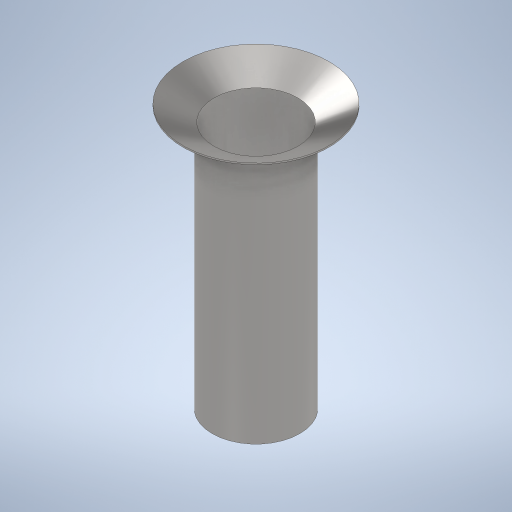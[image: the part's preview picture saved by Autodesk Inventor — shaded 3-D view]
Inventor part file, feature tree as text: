
AUTODESK INVENTOR PART (.ipt)
format: ipt  version: 2023 (Build 270158000, 158)  size: 261,632 bytes
history: native  units: in
note: dims shown in document units (in); Inventor stores cm internally (conversion verified against a paired STEP export)
features: sketch x3, extrude x2, other x1, plane x1, revolve x1
ambient origin geometry x8: Origin, YZ Plane, XZ Plane, XY Plane, X Axis, Y Axis, Z Axis, Center Point
bodies: Solid1 (feature_tree)
feature tree (8):
  sketch  "Sketch1"  dims[d0=12.0in d1=0.25in]
  extrude  "Extrusion1"  Depth=0.25in
  extrude  "Extrusion2"  Depth=0.25in TaperAngle=0.0deg
  other  "Work Axis1"
  sketch  "Sketch2"  dims[d2=34.0in d3=0.0in d4=0.25in d5=0.0in]
  plane  "Work Plane1"
  revolve  "Revolution1"  [1 undecoded]
  sketch  "Sketch3"  dims[d6=2.2in d7=4.0in d8=0.2in d9=90.0deg]
note: 1 required parameter value undecoded (feature->parameter linkage not recoverable at this tier; creation-order binding heuristic only, values carry confidence <= 0.55)
